# Revit family: C54
name_source: partatom
category: Lighting Fixtures
units: mm (PartAtom-declared; Revit-internal decimal feet)

## family parameters
Cut with Voids When Loaded = No
Host = Face
Light Source = Yes
OmniClass Number = 23.80.70.14
OmniClass Title = Luminaries for External Lighting
Part Type = Normal
Room Calculation Point = No
Round Connector Dimension = Use Diameter
Shared = No

## types (1)
- C54
    Apparent Load = 11 VA
    Color Filter = 16777215
    Default Elevation = 4' - 0"
    Description = Well lights withstand the corrosive forces of water, soil and time. C54 is now available with an IP68 rated energy efficient 11W LED light engine.
    Dimming Lamp Color Temperature Shift = <None>
    Emit Shape Visible in Rendering = No
    Emit from Rectangle Length = 0' - 6"
    Emit from Rectangle Width = 0' - 6"
    Lamp = LED
    Manufacturer = Kim Lighting
    Model = C54
    Photometric Web File = c54f3-9l3k.ies
    Tilt Angle = 90.00°
    Type Comments = Well Light
    URL = https://www.currentlighting.com
    Warranty = Limited 5 Years Warranty
    Wattage Comments = 11W

## geometry (parser evidence)
native form markers: Sweep x3
no freeform markers — native parametric forms only
